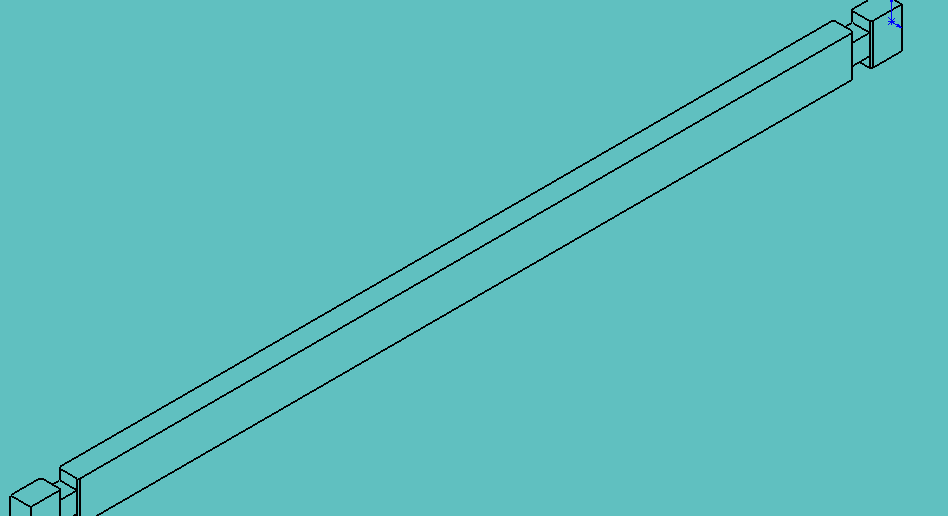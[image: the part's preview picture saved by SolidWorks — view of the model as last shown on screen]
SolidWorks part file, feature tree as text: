
SOLIDWORKS PART (.sldprt)
format: sldprt  version: not decoded by parser v0  size: 347,648 bytes
history: native  units: mm
features: sketch x5, cut_extrude x4, material x1, extrude x1 (+13 scaffold rows collapsed)
feature tree (24):
  scaffold x13  (default folders/planes/origin — collapsed)
  material  "Material <not specified>"
  sketch  "Sketch1"  dims[D1=140.0mm D2=70.0mm D3=35.0mm D4=70.0mm]
  extrude  "Extrude1"  Depth=3000mm
  sketch  "Sketch2"  dims[c1.D1=70.0mm c1.D2=60.0mm c1.D3=5.0mm c1.D4=60.0mm c1.D5=70.0mm c1.D6=5.0mm c1.D7=100.0mm c1.D8=100.0mm c1.D9=5.0mm c2.D9=45.0deg c2.D10=5.0mm c3.D10=45.0deg c4.D10=~6.941966mm c5.D10=45.0deg]
  cut_extrude  "Cut-Extrude1"  [1 undecoded]
  sketch  "Sketch3"  dims[D1=35.0mm D2=35.0mm]
  cut_extrude  "Cut-Extrude2"  [1 undecoded]
  sketch  "Sketch4"  dims[c1.D1=100.0mm c1.D2=5.0mm c1.D3=60.0mm c1.D4=70.0mm c1.D5=70.0mm c1.D6=60.0mm c1.D7=5.0mm c1.D8=100.0mm c1.D9=5.0mm c2.D9=~44.999978deg c3.D9=~7.071065mm c4.D9=~45.000022deg c5.D9=~7.071071mm c6.D9=~135.000022deg c7.D9=~7.071065mm c8.D9=~45.000022deg c9.D9=~7.071071mm c10.D9=~44.999978deg]
  cut_extrude  "Cut-Extrude3"  [1 undecoded]
  sketch  "Sketch5"  dims[D1=35.0mm D2=35.0mm]
  cut_extrude  "Cut-Extrude4"  [1 undecoded]
decode coverage: 6 of 10 modeling features carry decoded parameters
note: ~ marks probable driven/reference dimensions
note: 4 parameter values undecoded
summary: no parameter record found for 4 features
note: suppression state not decoded; provenance and decode notes live in map.json
